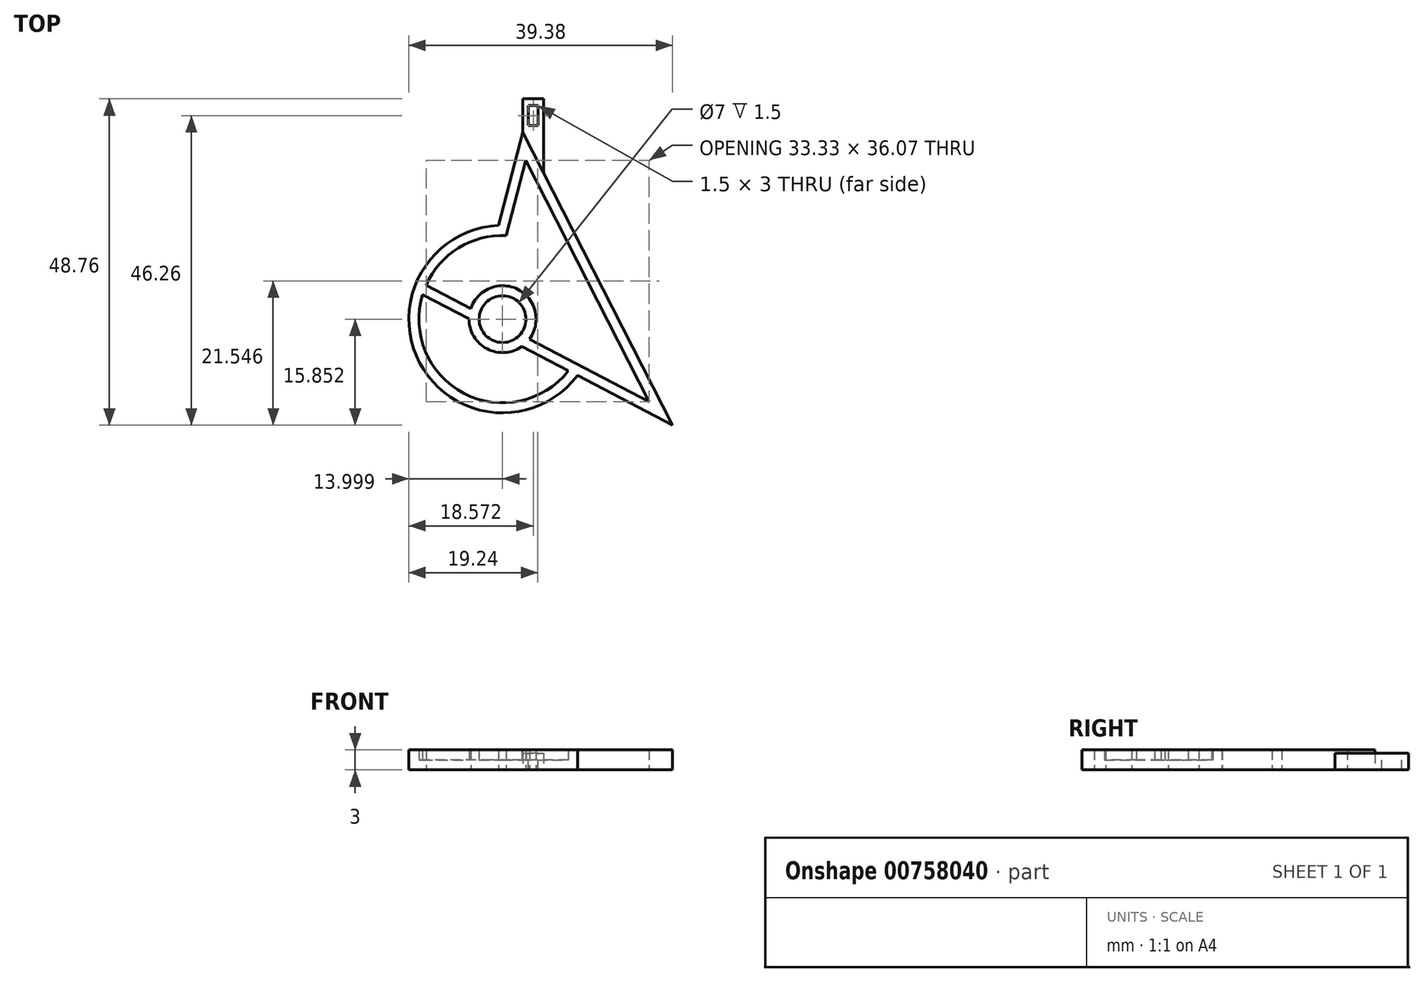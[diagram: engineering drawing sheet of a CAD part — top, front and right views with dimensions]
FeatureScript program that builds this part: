
annotation { "Feature Type Name" : "Feature", "Feature Type Description" : "" }
export const myFeature = defineFeature(function(context is Context, id is Id, definition is map)
    precondition{}
    {
        {
            var Q0;
            Q0=qCreatedBy(makeId("Front.planeOp"),FACE);
            var sketch = newSketch(context, id + "F0", { "sketchPlane" : qUnion([Q0])});
            skLineSegment(sketch, "E0", {"start": v(-25, 0) * mm, "end": v(25, 0) * mm, "construction": true});
            skLineSegment(sketch, "E1", {"start": v(0, 25) * mm, "end": v(0, -25) * mm, "construction": true});
            skArc(sketch, "E2", {"start": v(-17.53, 1) * mm, "mid": v(-12.7, -4.54) * mm, "end": v(-5.58, -6.4) * mm});
            skArc(sketch, "E3", {"start": v(-10.85, 4.5) * mm, "mid": v(-3.8, 1.65) * mm, "end": v(-2.1, 9.07) * mm});
            skCircle(sketch, "E4", {"center": v(-6.11, 6.08) * mm, "radius": 3.5 * mm});
            skLineSegment(sketch, "E5", {"start": v(-6.74, -7.9) * mm, "end": v(-3.07, -21.83) * mm});
            skLineSegment(sketch, "E6", {"start": v(-3.07, -21.83) * mm, "end": v(19.27, 21.93) * mm});
            skLineSegment(sketch, "E7", {"start": v(-17.53, 1) * mm, "end": v(-10.85, 4.5) * mm});
            skPoint(sketch, "E8.orphan", {"position": v(4.97, 11.87) * mm});
            skPoint(sketch, "E9.start.orphan", {"position": v(-17.19, 0.29) * mm});
            skLineSegment(sketch, "E10", {"start": v(-18.06, 2.42) * mm, "end": v(-11.11, 6.05) * mm});
            skLineSegment(sketch, "E11", {"start": v(5.07, 14.5) * mm, "end": v(19.27, 21.93) * mm});
            skLineSegment(sketch, "E12", {"start": v(-5.2, -7.89) * mm, "end": v(-2.62, -17.65) * mm});
            skLineSegment(sketch, "E13", {"start": v(-2.62, -17.65) * mm, "end": v(-5.58, -6.4) * mm});
            skLineSegment(sketch, "E14", {"start": v(4.58, 12.56) * mm, "end": v(15.8, 18.42) * mm});
            skLineSegment(sketch, "E15", {"start": v(-1.78, -16) * mm, "end": v(2.08, -8.43) * mm});
            skLineSegment(sketch, "E16", {"start": v(2.08, -8.43) * mm, "end": v(-2.62, -17.65) * mm});
            skLineSegment(sketch, "E17", {"start": v(2.08, -8.43) * mm, "end": v(15.8, 18.42) * mm});
            skArc(sketch, "E18.trimOffspring", {"start": v(5.07, 14.5) * mm, "mid": v(-18.5, 12.6) * mm, "end": v(-6.74, -7.9) * mm});
            skArc(sketch, "E19.trimOffspring", {"start": v(3.72, 13.8) * mm, "mid": v(-11.9, 17.16) * mm, "end": v(-18.06, 2.42) * mm});
            skLineSegment(sketch, "E20.trimOffspring", {"start": v(-3.23, 10.17) * mm, "end": v(3.72, 13.8) * mm});
            skLineSegment(sketch, "E21.trimOffspring", {"start": v(-2.1, 9.07) * mm, "end": v(4.58, 12.56) * mm});
            skArc(sketch, "E22.trimOffspring", {"start": v(-3.23, 10.17) * mm, "mid": v(-8.43, 10.51) * mm, "end": v(-11.11, 6.05) * mm});
            skLineSegment(sketch, "E23", {"start": v(-3.07, -21.83) * mm, "end": v(-3.07, -26.83) * mm});
            skLineSegment(sketch, "E24", {"start": v(-3.07, -26.83) * mm, "end": v(0, -26.83) * mm});
            skLineSegment(sketch, "E25", {"start": v(0, -26.83) * mm, "end": v(0, -15.8) * mm});
            skSolve(sketch);
        }
        {
            var Q0;
            {var subQ8=sQuery(id+"F0.wireOp",EDGE,"E2");Q0=makeQuery(id+"F0.imprint","IMPRINT",FACE,{"disambiguationData":[TD([[makeQuery(id+"F0.imprint","IMPRINT",EDGE,{"derivedFrom":subQ8}),-1.0]])]});}
            var Q1;
            Q1=sQuery(id+"F0.wireOp",EDGE,"E18.trimOffspring");
            var Q2;
            Q2=sQuery(id+"F0.wireOp",EDGE,"E5");
            var Q3;
            Q3=sQuery(id+"F0.wireOp",EDGE,"E6");
            var Q4;
            Q4=sQuery(id+"F0.wireOp",EDGE,"E13");
            var Q5;
            Q5=sQuery(id+"F0.wireOp",EDGE,"E16");
            var Q6;
            Q6=sQuery(id+"F0.wireOp",EDGE,"E17");
            var Q7;
            Q7=sQuery(id+"F0.wireOp",EDGE,"E2");
            var Q8;
            Q8=sQuery(id+"F0.wireOp",EDGE,"E7");
            var Q9;
            Q9=sQuery(id+"F0.wireOp",EDGE,"E19.trimOffspring");
            var Q10;
            Q10=sQuery(id+"F0.wireOp",EDGE,"E10");
            var Q11;
            Q11=sQuery(id+"F0.wireOp",EDGE,"E3");
            var Q12;
            Q12=sQuery(id+"F0.wireOp",EDGE,"E22.trimOffspring");
            var Q13;
            Q13=sQuery(id+"F0.wireOp",EDGE,"E4");
            var Q14;
            Q14=sQuery(id+"F0.wireOp",EDGE,"E21.trimOffspring");
            var Q15;
            Q15=sQuery(id+"F0.wireOp",EDGE,"E20.trimOffspring");
            var Q16;
            Q16=sQuery(id+"F0.wireOp",EDGE,"E14");
            var Q17;
            Q17=sQuery(id+"F0.wireOp",EDGE,"E11");
            extrude(context, id + "F1", {"entities" : qUnion([Q0]), "surfaceEntities" : qUnion([Q1, Q2, Q3, Q4, Q5, Q6, Q7, Q8, Q9, Q10, Q11, Q12, Q13, Q14, Q15, Q16, Q17]), "oppositeDirection" : true, "depth" : 3 * mm, "offsetDistance" : 25 * mm});
        }
        {
            var Q0;
            Q0=makeQuery(id+"F0.imprint","IMPRINT",FACE,{"disambiguationData":[TD([[makeQuery(id+"F0.imprint","IMPRINT",EDGE,{"derivedFrom":sQuery(id+"F0.wireOp",EDGE,"E10")}),1.0]])]});
            var Q1;
            Q1=makeQuery(id+"F0.imprint","IMPRINT",FACE,{"disambiguationData":[TD([[makeQuery(id+"F0.imprint","IMPRINT",EDGE,{"derivedFrom":sQuery(id+"F0.wireOp",EDGE,"E4")}),1.0]])]});
            extrude(context, id + "F2", {"entities" : qUnion([Q0, Q1]), "operationType" : NewBodyOperationType.ADD, "oppositeDirection" : true, "depth" : 1.5 * mm, "offsetDistance" : 25 * mm});
        }
        {
            var Q0;
            {var subQ0=sQuery(id+"F0.wireOp",EDGE,"E23");Q0=makeQuery(id+"F0.imprint","IMPRINT",FACE,{"disambiguationData":[TD([[makeQuery(id+"F0.imprint","IMPRINT",EDGE,{"derivedFrom":subQ0}),1.0]])]});}
            extrude(context, id + "F3", {"entities" : qUnion([Q0]), "operationType" : NewBodyOperationType.ADD, "oppositeDirection" : true, "depth" : 2.5 * mm, "offsetDistance" : 25 * mm});
        }
        {
            var Q0;
            Q0=makeQuery(id+"F3.opExtrude","CAP_FACE",FACE,{"disambiguationData":[OSD([sQuery(id+"F0.wireOp",EDGE,"E6"),sQuery(id+"F0.wireOp",EDGE,"E23"),sQuery(id+"F0.wireOp",EDGE,"E24"),sQuery(id+"F0.wireOp",EDGE,"E25")])],"isStart":false});
            var sketch = newSketch(context, id + "F4", { "sketchPlane" : qUnion([Q0])});
            skLineSegment(sketch, "E26.bottom", {"start": v(0.79, -25.83) * mm, "end": v(2.29, -25.83) * mm});
            skLineSegment(sketch, "E26.top", {"start": v(0.79, -22.83) * mm, "end": v(2.29, -22.83) * mm});
            skLineSegment(sketch, "E26.left", {"start": v(0.79, -25.83) * mm, "end": v(0.79, -22.83) * mm});
            skLineSegment(sketch, "E26.right", {"start": v(2.29, -25.83) * mm, "end": v(2.29, -22.83) * mm});
            skPoint(sketch, "E27.end.orphan", {"position": v(1.54, -25.83) * mm});
            skPoint(sketch, "E27.start.orphan", {"position": v(1.54, -26.83) * mm});
            skSolve(sketch);
        }
        {
            var Q0;
            Q0 = qSketchRegion(id + "F4", true);
            extrude(context, id + "F5", {"entities" : qUnion([Q0]), "operationType" : NewBodyOperationType.REMOVE, "oppositeDirection" : true, "depth" : 25 * mm, "offsetDistance" : 25 * mm});
        }
        {
            var Q0;
            Q0=makeQuery(id+"F1.opExtrude","SWEPT_BODY",BODY,{"disambiguationData":[OSD([sQuery(id+"F0.wireOp",EDGE,"E2"),sQuery(id+"F0.wireOp",EDGE,"E3"),sQuery(id+"F0.wireOp",EDGE,"E4"),sQuery(id+"F0.wireOp",EDGE,"E5"),sQuery(id+"F0.wireOp",EDGE,"E6"),sQuery(id+"F0.wireOp",EDGE,"E7"),sQuery(id+"F0.wireOp",EDGE,"E10"),sQuery(id+"F0.wireOp",EDGE,"E11"),sQuery(id+"F0.wireOp",EDGE,"E13"),sQuery(id+"F0.wireOp",EDGE,"E14"),sQuery(id+"F0.wireOp",EDGE,"E16"),sQuery(id+"F0.wireOp",EDGE,"E17"),sQuery(id+"F0.wireOp",EDGE,"E18.trimOffspring"),sQuery(id+"F0.wireOp",EDGE,"E19.trimOffspring"),sQuery(id+"F0.wireOp",EDGE,"E20.trimOffspring"),sQuery(id+"F0.wireOp",EDGE,"E21.trimOffspring"),sQuery(id+"F0.wireOp",EDGE,"E22.trimOffspring")])]});
            var Q1;
            Q1=makeQuery(id+"F3.opExtrude","CAP_EDGE",EDGE,{"disambiguationData":[OSD([sQuery(id+"F0.wireOp",EDGE,"E24")])],"isStart":true});
            transform(context, id + "F6", {"entities" : qUnion([Q0]), "transformType" : TransformType.ROTATION, "transformAxis" : qUnion([Q1]), "angle" : 90 * degree, "makeCopy" : false});
        }
    });
